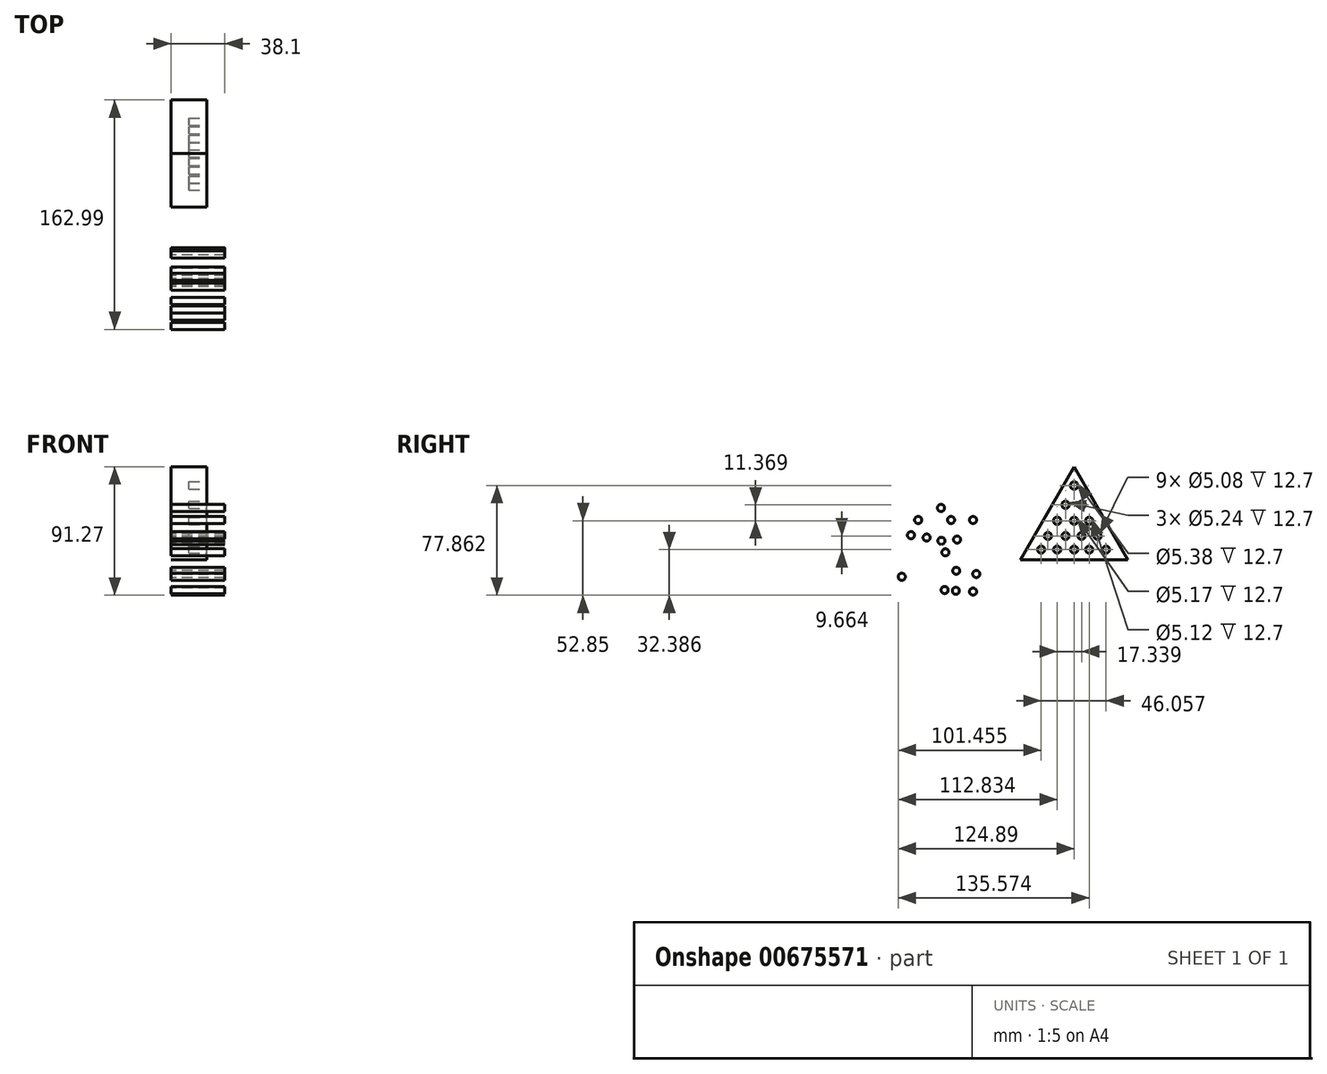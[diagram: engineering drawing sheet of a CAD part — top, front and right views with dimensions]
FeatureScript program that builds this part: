
annotation { "Feature Type Name" : "Feature", "Feature Type Description" : "" }
export const myFeature = defineFeature(function(context is Context, id is Id, definition is map)
    precondition{}
    {
        {
            var Q0;
            Q0=qCreatedBy(makeId("Right.planeOp"),FACE);
            var sketch = newSketch(context, id + "F0", { "sketchPlane" : qUnion([Q0])});
            skLineSegment(sketch, "E0", {"start": v(-76.2, 0) * mm, "end": v(-38.1, 66) * mm});
            skLineSegment(sketch, "E1", {"start": v(-38.1, 66) * mm, "end": v(0, 0) * mm});
            skLineSegment(sketch, "E2", {"start": v(-76.2, 0) * mm, "end": v(0, 0) * mm});
            skSolve(sketch);
        }
        {
            var Q0;
            Q0=makeQuery(id+"F0.imprint","IMPRINT",FACE,{"disambiguationData":[TD([[makeQuery(id+"F0.imprint","IMPRINT",EDGE,{"derivedFrom":sQuery(id+"F0.wireOp",EDGE,"E0")}),-1.0]])]});
            extrude(context, id + "F1", {"entities" : qUnion([Q0]), "depth" : 25.4 * mm, "offsetDistance" : 25.4 * mm});
        }
        {
            var Q0;
            Q0=makeQuery(id+"F1.opExtrude","CAP_FACE",FACE,{"disambiguationData":[OSD([sQuery(id+"F0.wireOp",EDGE,"E0"),sQuery(id+"F0.wireOp",EDGE,"E1"),sQuery(id+"F0.wireOp",EDGE,"E2")])],"isStart":false});
            var sketch = newSketch(context, id + "F2", { "sketchPlane" : qUnion([Q0])});
            skCircle(sketch, "E3", {"center": v(-61.54, 7.1) * mm, "radius": 2.54 * mm});
            skCircle(sketch, "E4", {"center": v(-50.16, 7.1) * mm, "radius": 2.54 * mm});
            skCircle(sketch, "E5", {"center": v(-38.1, 7.1) * mm, "radius": 2.54 * mm});
            skCircle(sketch, "E6", {"center": v(-27.42, 7.1) * mm, "radius": 2.54 * mm});
            skCircle(sketch, "E7", {"center": v(-15.48, 7.1) * mm, "radius": 2.54 * mm});
            skCircle(sketch, "E8", {"center": v(-56.7, 16.77) * mm, "radius": 2.54 * mm});
            skCircle(sketch, "E9", {"center": v(-44.19, 16.77) * mm, "radius": 2.54 * mm});
            skCircle(sketch, "E10", {"center": v(-32.82, 16.77) * mm, "radius": 2.54 * mm});
            skCircle(sketch, "E11", {"center": v(-21.45, 16.77) * mm, "radius": 2.54 * mm});
            skCircle(sketch, "E12", {"center": v(-50.16, 27.57) * mm, "radius": 2.62 * mm});
            skCircle(sketch, "E13", {"center": v(-38.1, 27.57) * mm, "radius": 2.58 * mm});
            skCircle(sketch, "E14", {"center": v(-27.42, 27.57) * mm, "radius": 2.56 * mm});
            skCircle(sketch, "E15", {"center": v(-44.19, 38.94) * mm, "radius": 2.62 * mm});
            skCircle(sketch, "E16", {"center": v(-32.82, 38.94) * mm, "radius": 2.62 * mm});
            skCircle(sketch, "E17", {"center": v(-38.1, 52.58) * mm, "radius": 2.7 * mm});
            skSolve(sketch);
        }
        {
            var Q0;
            Q0 = qSketchRegion(id + "F2", true);
            extrude(context, id + "F3", {"entities" : qUnion([Q0]), "operationType" : NewBodyOperationType.REMOVE, "oppositeDirection" : true, "depth" : 12.7 * mm, "offsetDistance" : 25.4 * mm});
        }
        {
            var Q0;
            Q0=qCreatedBy(makeId("Right.planeOp"),FACE);
            var sketch = newSketch(context, id + "F4", { "sketchPlane" : qUnion([Q0])});
            skCircle(sketch, "E18", {"center": v(-130.03, -21.6) * mm, "radius": 2.54 * mm});
            skCircle(sketch, "E19", {"center": v(-122.08, -22.17) * mm, "radius": 2.54 * mm});
            skCircle(sketch, "E20", {"center": v(-109.85, -22.74) * mm, "radius": 2.54 * mm});
            skCircle(sketch, "E21", {"center": v(-121.8, -7.96) * mm, "radius": 2.54 * mm});
            skCircle(sketch, "E22", {"center": v(-160.45, -12.22) * mm, "radius": 2.54 * mm});
            skCircle(sketch, "E23", {"center": v(-107.58, -10.23) * mm, "radius": 2.54 * mm});
            skCircle(sketch, "E24", {"center": v(-129.47, 5.12) * mm, "radius": 2.54 * mm});
            skCircle(sketch, "E25", {"center": v(-153.9, 17.34) * mm, "radius": 2.54 * mm});
            skCircle(sketch, "E26", {"center": v(-142.82, 15.63) * mm, "radius": 2.54 * mm});
            skCircle(sketch, "E27", {"center": v(-132.3, 13.36) * mm, "radius": 2.54 * mm});
            skCircle(sketch, "E28", {"center": v(-121.22, 14.21) * mm, "radius": 2.54 * mm});
            skCircle(sketch, "E29", {"center": v(-148.8, 28.14) * mm, "radius": 2.54 * mm});
            skCircle(sketch, "E30", {"center": v(-132.6, 36.67) * mm, "radius": 2.54 * mm});
            skCircle(sketch, "E31", {"center": v(-125.49, 28.14) * mm, "radius": 2.54 * mm});
            skCircle(sketch, "E32", {"center": v(-109.85, 28.14) * mm, "radius": 2.54 * mm});
            skSolve(sketch);
        }
        {
            var Q0;
            Q0 = qSketchRegion(id + "F4", true);
            extrude(context, id + "F5", {"entities" : qUnion([Q0]), "depth" : 38.1 * mm, "offsetDistance" : 25.4 * mm});
        }
    });
